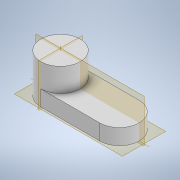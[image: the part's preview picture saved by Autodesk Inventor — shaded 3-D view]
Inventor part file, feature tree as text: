
AUTODESK INVENTOR PART (.ipt)
format: ipt  version: 2022.4 (Build 264492010, 492A)  size: 116,224 bytes
history: native  units: mm
features: extrude x2, sketch x1
ambient origin geometry x8: Origin, YZ Plane, XZ Plane, XY Plane, X Axis, Y Axis, Z Axis, Center Point
bodies: Solid1 (feature_tree)
feature tree (3):
  sketch  "Sketch1"  dims[d0=5.0mm d1=7.5mm d3=5.0mm d4=0.0mm d5=2.0mm d6=0.0mm d13=7.5mm d14=5.0mm]
  extrude  "Extrusion1"  Depth=7.5mm
  extrude  "Extrusion2"  Depth=5.0mm TaperAngle=0.0deg
